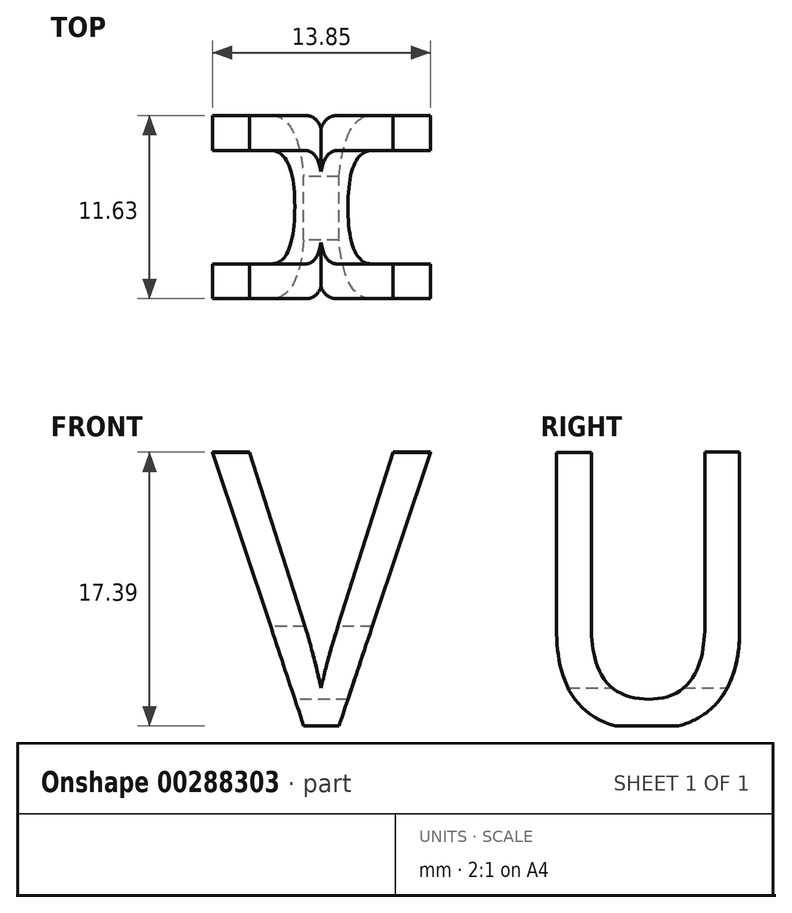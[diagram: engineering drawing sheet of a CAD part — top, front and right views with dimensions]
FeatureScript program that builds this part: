
annotation { "Feature Type Name" : "Feature", "Feature Type Description" : "" }
export const myFeature = defineFeature(function(context is Context, id is Id, definition is map)
    precondition{}
    {
        {
            var Q0;
            Q0=qCreatedBy(makeId("Front.planeOp"),FACE);
            var sketch = newSketch(context, id + "F0", { "sketchPlane" : qUnion([Q0])});
            skText(sketch, "E0", { "text": "V", "fontName": "DroidSansMono.ttf"});
            const initialGuessF0  = {"E0": [0, 0, 1, 0, 0.01767]};
            skSetInitialGuess(sketch, initialGuessF0);
            skSolve(sketch);
        }
        {
            var Q0;
            Q0 = qSketchRegion(id + "F0", true);
            extrude(context, id + "F1", {"entities" : qUnion([Q0]), "depth" : 25.4 * mm});
        }
        {
            var Q0;
            Q0=qCreatedBy(makeId("Right.planeOp"),FACE);
            var sketch = newSketch(context, id + "F2", { "sketchPlane" : qUnion([Q0])});
            skLineSegment(sketch, "E1.0", {"start": v(-25.4, 17.52) * mm, "end": v(0, 17.52) * mm});
            skLineSegment(sketch, "E2.0", {"start": v(0, 0) * mm, "end": v(0, 17.52) * mm});
            skLineSegment(sketch, "E3.0", {"start": v(-25.4, 0) * mm, "end": v(0, 0) * mm});
            skLineSegment(sketch, "E4.0", {"start": v(-25.4, 0) * mm, "end": v(-25.4, 17.52) * mm});
            skText(sketch, "E5", { "text": "U", "fontName": "DroidSansMono.ttf"});
            const initialGuessF2  = {"E5": [-0.0254, 0, 1, 0, 0.01752]};
            skSetInitialGuess(sketch, initialGuessF2);
            skSolve(sketch);
        }
        {
            var Q0;
            Q0=makeQuery(id+"F2.imprint","IMPRINT",FACE,{"disambiguationData":[TD([[makeQuery(id+"F2.imprint","IMPRINT",EDGE,{"derivedFrom":sQuery(id+"F2.wireOp",EDGE,"E5.sketch_text.stroke-0")}),-1.0]])]});
            extrude(context, id + "F3", {"entities" : qUnion([Q0]), "operationType" : NewBodyOperationType.INTERSECT, "depth" : 25.4 * mm});
        }
    });
